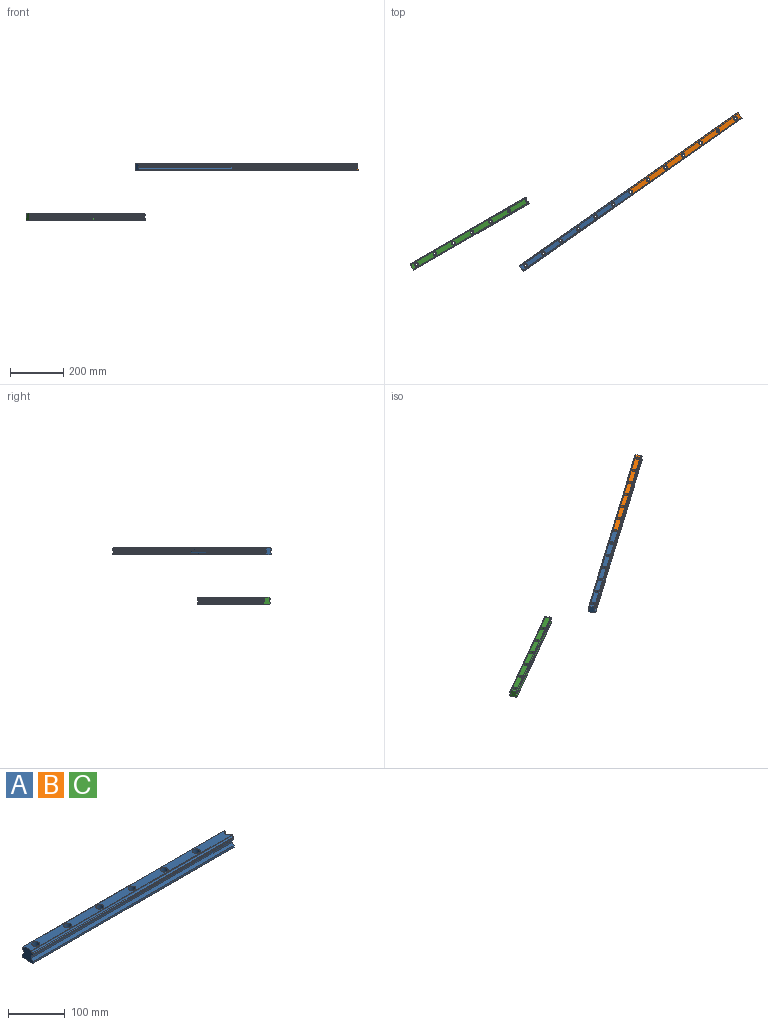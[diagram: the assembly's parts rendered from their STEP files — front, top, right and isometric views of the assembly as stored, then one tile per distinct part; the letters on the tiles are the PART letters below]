
ASSEMBLY  parts=3 mates=1
PART A: 74 faces, bbox 500.2x28.2x26.1 mm
  f0: plane 73.92x6.65mm, normal (0,0,-1), area 467.1mm2, adj f9,f10,f11,f12
  f1: plane 73.92x6.65mm, normal (0,0,-1), area 467.1mm2, adj f8,f12,f13,f14
  f2: plane 73.92x6.65mm, normal (0,0,-1), area 467.1mm2, adj f7,f14,f15,f16
  f3: plane 73.92x6.65mm, normal (0,0,-1), area 467.1mm2, adj f6,f16,f17,f18
  f4: plane 73.92x6.65mm, normal (0,0,-1), area 467.1mm2, adj f5,f18,f19,f44
  f5: plane 75.05x0.53mm, normal (0,0.71,-0.71), area 52.5mm2, adj f4,f18,f44,f52
  f6: plane 75.05x0.53mm, normal (0,0.71,-0.71), area 52.5mm2, adj f3,f16,f18,f52
  f7: plane 75.05x0.53mm, normal (0,0.71,-0.71), area 52.5mm2, adj f2,f14,f16,f52
  f8: plane 75.05x0.53mm, normal (0,0.71,-0.71), area 52.5mm2, adj f1,f12,f14,f52
  f9: plane 75.05x0.53mm, normal (0,0.71,-0.71), area 52.5mm2, adj f0,f10,f12,f52
  f10: cylinder r=4.5mm len=14mm, axis (0,0,1), area 389.8mm2, adj f0,f9,f11,f50,f52,f53,f54,f55
  f11: plane 75.05x0.53mm, normal (0,-0.71,-0.71), area 52.5mm2, adj f0,f10,f12,f56
  f12: cylinder r=4.5mm len=14mm, axis (0,0,1), area 389.8mm2, adj f0,f1,f8,f9,f11,f13,f49,f52
  f13: plane 75.05x0.53mm, normal (0,-0.71,-0.71), area 52.5mm2, adj f1,f12,f14,f56
  f14: cylinder r=4.5mm len=14mm, axis (0,0,1), area 389.8mm2, adj f1,f2,f7,f8,f13,f15,f48,f52
  f15: plane 75.05x0.53mm, normal (0,-0.71,-0.71), area 52.5mm2, adj f2,f14,f16,f56
  f16: cylinder r=4.5mm len=14mm, axis (0,0,1), area 389.8mm2, adj f2,f3,f6,f7,f15,f17,f47,f52
  f17: plane 75.05x0.53mm, normal (0,-0.71,-0.71), area 52.5mm2, adj f3,f16,f18,f56
  f18: cylinder r=4.5mm len=14mm, axis (0,0,1), area 389.8mm2, adj f3,f4,f5,f6,f17,f19,f46,f52
  f19: plane 75.05x0.53mm, normal (0,-0.71,-0.71), area 52.5mm2, adj f4,f18,f44,f56
  f20: cylinder r=2.93mm len=500mm, axis (1,0,0), area 2089.4mm2, adj f21,f60,f61,f62
  f21: plane 500x1.38mm, normal (0,0.71,0.71), area 979.1mm2, adj f20,f22,f60,f62
  f22: plane 500x2.43mm, normal (0,1,0), area 1215mm2, adj f21,f23,f60,f62
  f23: plane 500x1.38mm, normal (0,0.71,-0.71), area 972.2mm2, adj f22,f24,f60,f62
  f24: cylinder r=2.93mm len=500mm, axis (1,0,0), area 2099.1mm2, adj f23,f25,f60,f62
  f25: plane 500x0.6mm, normal (0,0.71,-0.71), area 427.1mm2, adj f24,f26,f60,f62
  f26: plane 500x3.98mm, normal (0,1,0), area 1990mm2, adj f25,f27,f60,f62
  f27: plane 500x4.8mm, normal (0,0.71,0.71), area 3394.4mm2, adj f26,f28,f60,f62
  f28: plane 500x3.8mm, normal (0,1,0), area 1899.8mm2, adj f27,f29,f60,f62
  f29: plane 500x1.5mm, normal (0,0.71,-0.71), area 1060.2mm2, adj f28,f30,f60,f62
  f30: plane 500x4.75mm, normal (0,0,-1), area 2375.7mm2, adj f29,f31,f60,f62
  f31: plane 500x0.5mm, normal (0,-0.71,-0.71), area 353.1mm2, adj f30,f52,f60,f62
  f32: cylinder r=2.93mm len=500mm, axis (1,0,0), area 2089.4mm2, adj f33,f62,f63,f64
  f33: plane 500x1.38mm, normal (0,-0.71,0.71), area 979.1mm2, adj f32,f34,f62,f64
  f34: plane 500x2.43mm, normal (0,-1,0), area 1215mm2, adj f33,f35,f62,f64
  f35: plane 500x1.38mm, normal (0,-0.71,-0.71), area 972.3mm2, adj f34,f36,f62,f64
  f36: cylinder r=2.93mm len=500mm, axis (1,0,0), area 2099.1mm2, adj f35,f37,f62,f64
  f37: plane 500x0.6mm, normal (0,-0.71,-0.71), area 427.1mm2, adj f36,f38,f62,f64
  f38: plane 500x3.98mm, normal (0,-1,0), area 1990mm2, adj f37,f39,f62,f64
  f39: plane 500x4.8mm, normal (0,-0.71,0.71), area 3394.4mm2, adj f38,f40,f62,f64
  f40: plane 500x3.8mm, normal (0,-1,0), area 1899.8mm2, adj f39,f41,f62,f64
  f41: plane 500x1.5mm, normal (0,-0.71,-0.71), area 1060.2mm2, adj f40,f42,f62,f64
  f42: plane 500x4.75mm, normal (0,0,-1), area 2375.7mm2, adj f41,f43,f62,f64
  f43: plane 500x0.5mm, normal (0,0.71,-0.71), area 353.1mm2, adj f42,f56,f62,f64
  f44: cylinder r=4.5mm len=14mm, axis (0,0,-1), area 194.9mm2, adj f4,f5,f19,f45,f52,f56,f60,f64
  f45: plane 14.22x7.25mm, normal (0,0,1), area 45.2mm2, adj f44,f59,f60,f64
  f46: plane 14.21x14.21mm, normal (0,0,1), area 90.2mm2, adj f18,f65
  f47: plane 14.21x14.21mm, normal (0,0,1), area 90.2mm2, adj f16,f66
  f48: plane 14.21x14.21mm, normal (0,0,1), area 90.2mm2, adj f14,f67
  f49: plane 14.21x14.21mm, normal (0,0,1), area 90.2mm2, adj f12,f68
  f50: plane 14.21x14.21mm, normal (0,0,1), area 90.2mm2, adj f10,f69
  f51: plane 17.54x0.53mm, normal (0,0.71,-0.71), area 12.1mm2, adj f52,f58,f62,f70
  f52: plane 500.09x3.59mm, normal (0,0,-1), area 1733.6mm2, adj f5,f6,f7,f8,f9,f10,f12,f14
  f53: plane 75.05x0.53mm, normal (0,0.71,-0.71), area 52.5mm2, adj f10,f52,f54,f70
  f54: plane 73.92x6.65mm, normal (0,0,-1), area 467.1mm2, adj f10,f53,f55,f70
  f55: plane 75.05x0.53mm, normal (0,-0.71,-0.71), area 52.5mm2, adj f10,f54,f56,f70
  f56: plane 500.09x3.59mm, normal (0,0,-1), area 1733.5mm2, adj f10,f11,f12,f13,f14,f15,f16,f17
  f57: plane 17.54x0.53mm, normal (0,-0.71,-0.71), area 12.1mm2, adj f56,f58,f62,f70
  f58: plane 17.03x6.65mm, normal (0,0,-1), area 103.6mm2, adj f51,f57,f62,f70
  f59: cylinder r=7mm len=14mm, axis (0,0,-1), area 261.7mm2, adj f45,f60,f64,f71
  f60: plane 25.9x9.5mm, normal (1,0,0), area 156mm2, adj f20,f21,f22,f23,f24,f25,f26,f27
  f61: plane 500x0.59mm, normal (0,0.71,0.71), area 420.5mm2, adj f20,f60,f62,f71
  f62: plane 28x25.9mm, normal (-1,0,0), area 603.7mm2, adj f20,f21,f22,f23,f24,f25,f26,f27
  f63: plane 500x0.59mm, normal (0,-0.71,0.71), area 420.5mm2, adj f32,f62,f64,f71
  f64: plane 25.9x9.5mm, normal (1,0,0), area 156.1mm2, adj f32,f33,f34,f35,f36,f37,f38,f39
  f65: cylinder r=7mm len=14mm, axis (0,0,1), area 523.4mm2, adj f46,f71
  f66: cylinder r=7mm len=14mm, axis (0,0,1), area 523.4mm2, adj f47,f71
  f67: cylinder r=7mm len=14mm, axis (0,0,1), area 523.4mm2, adj f48,f71
  f68: cylinder r=7mm len=14mm, axis (0,0,1), area 523.4mm2, adj f49,f71
  f69: cylinder r=7mm len=14mm, axis (0,0,1), area 523.4mm2, adj f50,f71
  f70: cylinder r=4.5mm len=14mm, axis (0,0,1), area 389.8mm2, adj f51,f52,f53,f54,f55,f56,f57,f58
  f71: plane 500.21x18.63mm, normal (0,0,1), area 8208.5mm2, adj f59,f60,f61,f62,f63,f64,f65,f66
  f72: plane 14.21x14.21mm, normal (0,0,1), area 90.2mm2, adj f70,f73
  f73: cylinder r=7mm len=14mm, axis (0,0,1), area 523.4mm2, adj f71,f72
PART B: same geometry as A
PART C: same geometry as A
PLACE A rot(axis=(0,0,1),35deg) t=(-444.77,-706.86,111.8)mm
PLACE B rot(axis=(0,0,-1),145deg) t=(341.61,-156.22,111.8)mm
PLACE C rot(axis=(0,0,1),30deg) t=(-854.52,-702.5,-73.32)mm
MATE planar A.f42 <-> B.f30  axis (0,0,-1) through (-45.77,-439.84,111.8)mm
